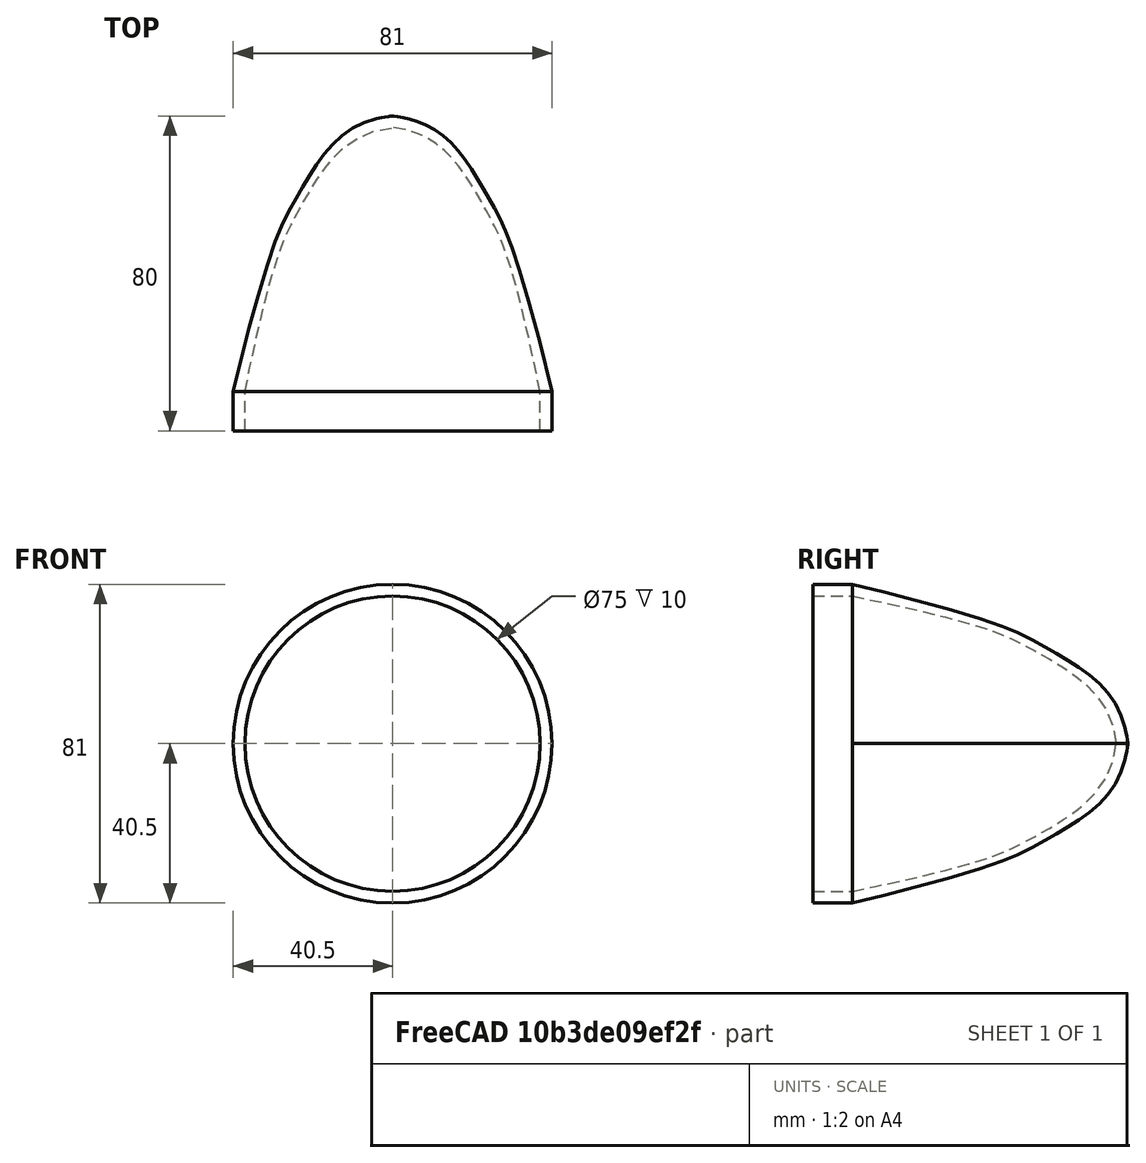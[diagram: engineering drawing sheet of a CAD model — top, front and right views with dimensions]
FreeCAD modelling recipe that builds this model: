
FCSTD DOCUMENT  (FreeCAD 0.18R16131 (Git))
Label: S200_Head_v2
License: All rights reserved
LicenseURL: http://en.wikipedia.org/wiki/All_rights_reserved
objects: Sketcher::SketchObject×1, PartDesign::Revolution×1, PartDesign::Body×1
note: 4 computed .brp shape members not serialized (recipe doc carries the construction recipe); baked Part::Feature solids carry a one-line shape summary decoded from their .brp

FEATURE [Sketcher::SketchObject] Sketch
  MapMode = 5
  Support = -> [XY_Plane]
  sketch-geometry (24):
    g0: LineSegment StartX=37.5 StartY=50 StartZ=0 EndX=37.5 EndY=60 EndZ=0
    g1: LineSegment StartX=40.5 StartY=50 StartZ=0 EndX=40.5 EndY=60 EndZ=0
    g2-g7: Circle [constr] x6 (B-spline internal-alignment scaffolding for g8; pole/knot coordinates omitted)
    g8: BSplineCurve PolesCount=6 KnotsCount=4 Degree=3 IsPeriodic=0
    g9-g12: GeomPoint [constr] x4 (B-spline internal-alignment scaffolding for g8; pole/knot coordinates omitted)
    g13-g17: Circle [constr] x5 (B-spline internal-alignment scaffolding for g18; pole/knot coordinates omitted)
    g18: BSplineCurve PolesCount=5 KnotsCount=3 Degree=3 IsPeriodic=0
    g19: GeomPoint [constr] X=37.5 Y=60 Z=0
    g20: GeomPoint [constr] X=23.1565 Y=107.122 Z=0
    g21: GeomPoint [constr] X=0 Y=127 Z=0
    g22: LineSegment StartX=0 StartY=130 StartZ=0 EndX=0 EndY=127 EndZ=0
    g23: LineSegment StartX=37.5 StartY=50 StartZ=0 EndX=40.5 EndY=50 EndZ=0
  constraints (38):
    c: Vertical(g0)
    c: Vertical(g1)
    c: DistanceX(g0,g1) = 3
    c: Coincident(g8,g1)
    c: Radius(g2) = 3
    c: Equal(g2, g3-g6) x4
    c: PointOnObject(g6,g-2)
    c: Equal(g2,g7)
    c: Coincident(g8,g6)
    c: InternalAlignment(g2-g7 -> g8) x6
    c: InternalAlignment(g9-g12 -> g8) x4
    c: DistanceY(g1,g8) = 70
    c: DistanceY(g1,g3) = 37
    c: DistanceX(g3,g1) = 9
    c: DistanceY(g3,g4) = 10
    c: DistanceX(g4,g3) = 6
    c: DistanceY(g4,g5) = 22
    c: DistanceX(g5,g4) = 12
    c: Coincident(g18,g0)
    c: Radius(g13) = 6
    c: Equal(g13, g14-g17) x4
    c: PointOnObject(g18,g-2)
    c: InternalAlignment(g13-g17 -> g18) x5
    c: InternalAlignment(g19,g18)
    c: InternalAlignment(g20,g18)
    c: Distance(g14,g3) = 3
    c: Distance(g16,g5) = 3
    c: Distance(g18,g8) = 3
    c: Distance(g4,g15) = 3
    c: Coincident(g22,g8)
    c: Coincident(g22,g18)
    c: DistanceX(g-1,g1) = 40.5
    c: DistanceY(g0,g0) = 10
    c: Equal(g0,g1)
    c: DistanceY(g-1,g1) = 50
    c: Coincident(g23,g0)
    c: Coincident(g23,g1)
    c: Horizontal(g23)
FEATURE [PartDesign::Revolution] Revolution
  Angle = 360
  Axis = (1e-16,1,-1e-16)
  Base = (0,0,0)
  Profile = -> Sketch
  ReferenceAxis = -> Y_Axis
  Reversed = true
FEATURE [PartDesign::Body] Body
  Group = -> [Sketch,Revolution]
  Origin = -> Origin
  Tip = -> Revolution
